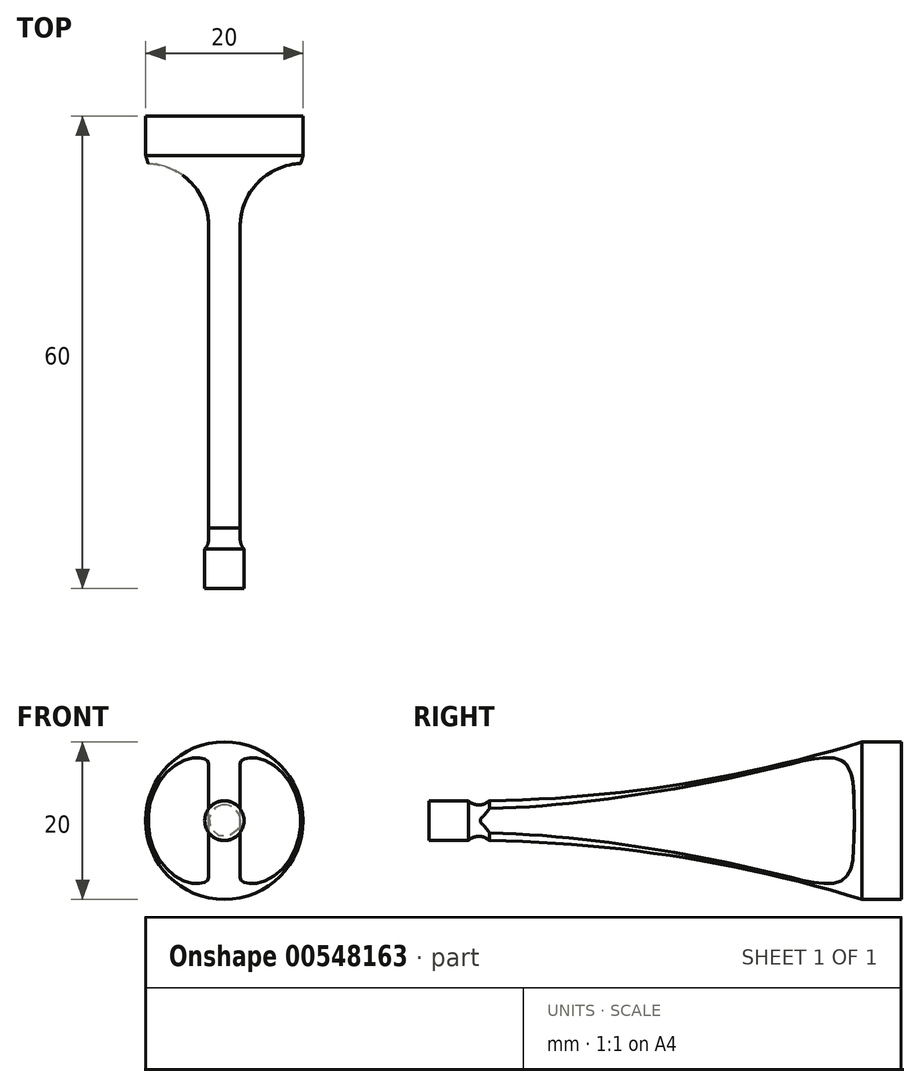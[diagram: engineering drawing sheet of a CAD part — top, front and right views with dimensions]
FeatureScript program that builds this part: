
annotation { "Feature Type Name" : "Feature", "Feature Type Description" : "" }
export const myFeature = defineFeature(function(context is Context, id is Id, definition is map)
    precondition{}
    {
        {
            var Q0;
            Q0=qCreatedBy(makeId("Right.planeOp"),FACE);
            var sketch = newSketch(context, id + "F0", { "sketchPlane" : qUnion([Q0])});
            skLineSegment(sketch, "E0", {"start": v(39.05, 0) * mm, "end": v(-78.02, 0) * mm, "construction": true});
            skLineSegment(sketch, "E1", {"start": v(0, 0) * mm, "end": v(0, 10) * mm});
            skLineSegment(sketch, "E2", {"start": v(0, 10) * mm, "end": v(-5, 10) * mm});
            skLineSegment(sketch, "E3", {"start": v(0, 0) * mm, "end": v(-60, 0) * mm});
            skLineSegment(sketch, "E4", {"start": v(-60, 0) * mm, "end": v(-60, 2.5) * mm});
            skLineSegment(sketch, "E5", {"start": v(-60, 2.5) * mm, "end": v(-55, 2.5) * mm});
            skArc(sketch, "E6", {"start": v(-52.33, 2.52) * mm, "mid": v(-28.4, 4.59) * mm, "end": v(-5, 10) * mm});
            skArc(sketch, "E7", {"start": v(-55, 2.5) * mm, "mid": v(-53.66, 2) * mm, "end": v(-52.33, 2.52) * mm});
            skSolve(sketch);
        }
        {
            var Q0;
            Q0 = qSketchRegion(id + "F0", true);
            var Q1;
            Q1=sQuery(id+"F0.wireOp",EDGE,"E0");
            revolve(context, id + "F1", {"entities" : qUnion([Q0]), "axis" : qUnion([Q1]), "revolveType" : RevolveType.FULL});
        }
        {
            var Q0;
            Q0=qCreatedBy(makeId("Top.planeOp"),FACE);
            var sketch = newSketch(context, id + "F2", { "sketchPlane" : qUnion([Q0])});
            skLineSegment(sketch, "E8", {"start": v(2, -53.5) * mm, "end": v(2, -14) * mm});
            skArc(sketch, "E9", {"start": v(10, -6) * mm, "mid": v(4.34, -8.34) * mm, "end": v(2, -14) * mm});
            skLineSegment(sketch, "E10", {"start": v(10, 2.45) * mm, "end": v(10, -6) * mm, "construction": true});
            skLineSegment(sketch, "E11", {"start": v(10, -53.5) * mm, "end": v(2, -53.5) * mm});
            skLineSegment(sketch, "E12", {"start": v(10, -53.5) * mm, "end": v(10, -6) * mm});
            skLineSegment(sketch, "E13", {"start": v(-2, -53.5) * mm, "end": v(-2, -14) * mm});
            skLineSegment(sketch, "E14", {"start": v(0, -71.6) * mm, "end": v(0, 17.57) * mm, "construction": true});
            skArc(sketch, "E15", {"start": v(-2, -14) * mm, "mid": v(-4.34, -8.34) * mm, "end": v(-10, -6) * mm});
            skLineSegment(sketch, "E16", {"start": v(-2, -53.5) * mm, "end": v(-10, -53.5) * mm});
            skLineSegment(sketch, "E17", {"start": v(-10, -53.5) * mm, "end": v(-10, -6) * mm});
            skSolve(sketch);
        }
        {
            var Q0;
            Q0 = qSketchRegion(id + "F2", true);
            var Q1;
            Q1=makeQuery(id+"F1.opRevolve","SWEPT_BODY",BODY,{"disambiguationData":[OSD([sQuery(id+"F0.wireOp",EDGE,"E1"),sQuery(id+"F0.wireOp",EDGE,"E2"),sQuery(id+"F0.wireOp",EDGE,"E3"),sQuery(id+"F0.wireOp",EDGE,"E4"),sQuery(id+"F0.wireOp",EDGE,"E5"),sQuery(id+"F0.wireOp",EDGE,"E6"),sQuery(id+"F0.wireOp",EDGE,"E7")])]});
            var Q2;
            Q2=makeQuery(id+"F1.opRevolve","SWEPT_BODY",BODY,{"disambiguationData":[OSD([sQuery(id+"F0.wireOp",EDGE,"E1"),sQuery(id+"F0.wireOp",EDGE,"E2"),sQuery(id+"F0.wireOp",EDGE,"E3"),sQuery(id+"F0.wireOp",EDGE,"E4"),sQuery(id+"F0.wireOp",EDGE,"E5"),sQuery(id+"F0.wireOp",EDGE,"E6"),sQuery(id+"F0.wireOp",EDGE,"E7")])]});
            extrude(context, id + "F3", {"entities" : qUnion([Q0]), "operationType" : NewBodyOperationType.REMOVE, "endBound" : BoundingType.THROUGH_ALL, "oppositeDirection" : true, "depth" : 25 * mm, "endBoundEntityBody" : qUnion([Q1]), "offsetDistance" : 100 * mm, "offsetOppositeDirection" : true, "hasSecondDirection" : true, "secondDirectionBound" : SecondDirectionBoundingType.UP_TO_BODY, "secondDirectionOppositeDirection" : false, "secondDirectionDepth" : 25 * mm, "secondDirectionBoundEntityBody" : qUnion([Q2])});
        }
    });
